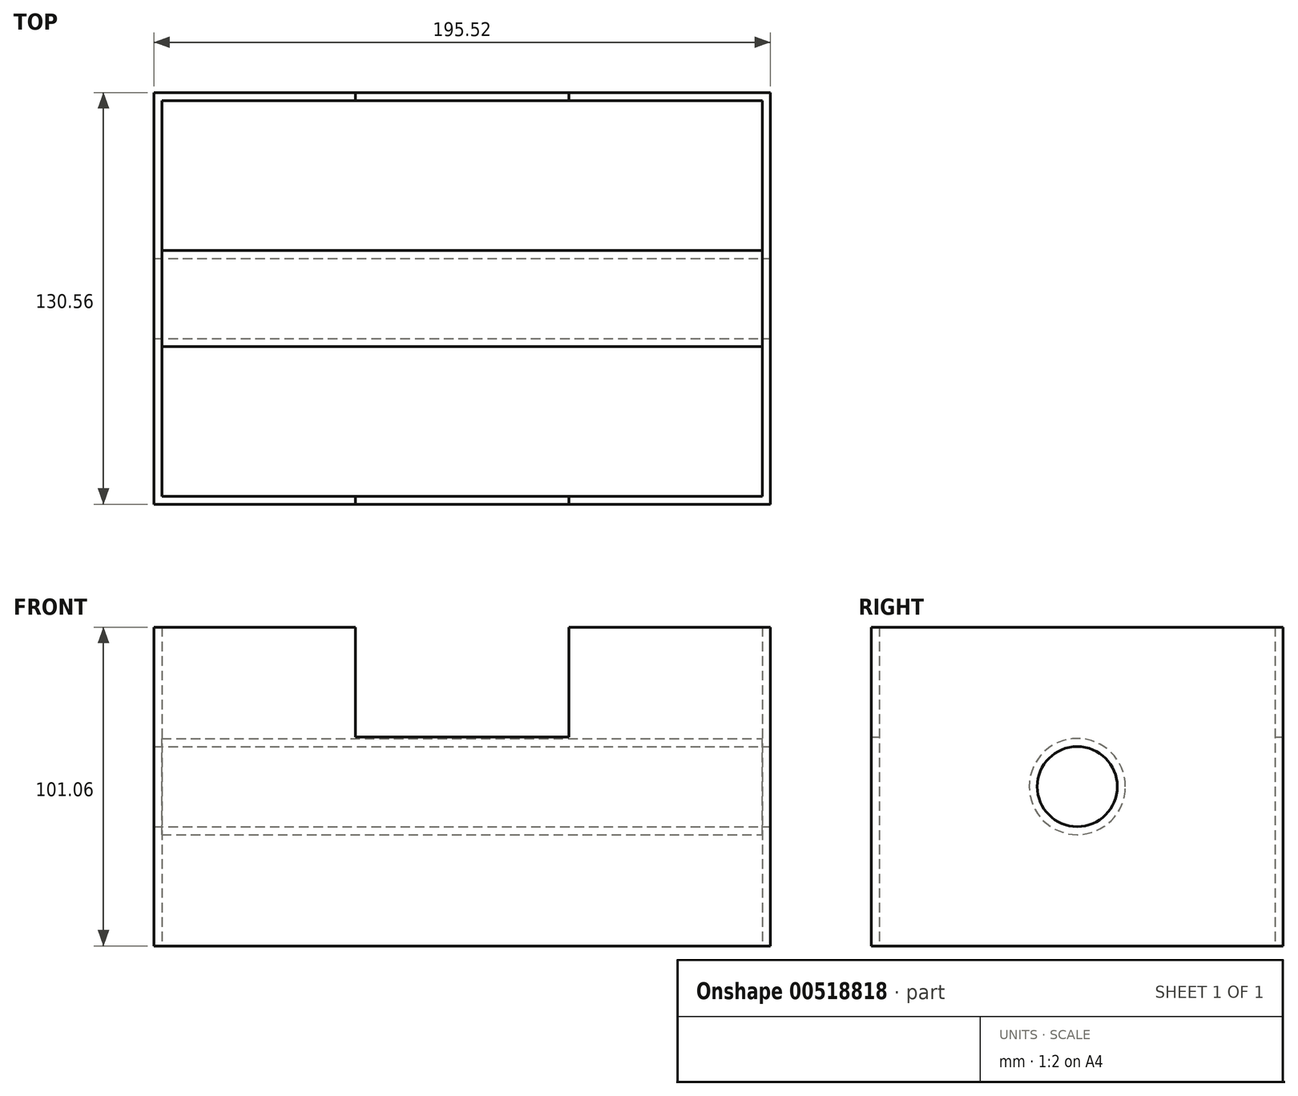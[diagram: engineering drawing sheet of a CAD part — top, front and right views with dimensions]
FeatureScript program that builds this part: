
annotation { "Feature Type Name" : "Feature", "Feature Type Description" : "" }
export const myFeature = defineFeature(function(context is Context, id is Id, definition is map)
    precondition{}
    {
        {
            var Q0;
            Q0=qCreatedBy(makeId("Front.planeOp"),FACE);
            var sketch = newSketch(context, id + "F0", { "sketchPlane" : qUnion([Q0])});
            skLineSegment(sketch, "E0.bottom", {"start": v(-97.76, 50.53) * mm, "end": v(-33.82, 50.53) * mm});
            skLineSegment(sketch, "E0.top", {"start": v(-97.76, -50.53) * mm, "end": v(97.76, -50.53) * mm});
            skLineSegment(sketch, "E0.left", {"start": v(-97.76, 50.53) * mm, "end": v(-97.76, -50.53) * mm});
            skLineSegment(sketch, "E0.right", {"start": v(97.76, 50.53) * mm, "end": v(97.76, -50.53) * mm});
            skPoint(sketch, "E0.middle", {"position": v(0, 0) * mm});
            skLineSegment(sketch, "E1.bottom", {"start": v(33.82, 50.53) * mm, "end": v(34.73, 50.53) * mm});
            skLineSegment(sketch, "E2.top", {"start": v(33.82, 15.69) * mm, "end": v(-33.9, 15.69) * mm});
            skLineSegment(sketch, "E2.left", {"start": v(33.82, 50.53) * mm, "end": v(33.82, 15.69) * mm});
            skLineSegment(sketch, "E2.right", {"start": v(-33.9, 50.53) * mm, "end": v(-33.9, 15.69) * mm});
            skLineSegment(sketch, "E3.trimOffspring", {"start": v(-33.82, 50.53) * mm, "end": v(-33.9, 50.53) * mm});
            skPoint(sketch, "E4.start.orphan", {"position": v(0, 50.53) * mm});
            skLineSegment(sketch, "E5.trimOffspring", {"start": v(34.73, 50.53) * mm, "end": v(97.76, 50.53) * mm});
            skSolve(sketch);
        }
        {
            var Q0;
            Q0 = qSketchRegion(id + "F0", true);
            extrude(context, id + "F1", {"entities" : qUnion([Q0]), "endBound" : BoundingType.SYMMETRIC, "depth" : 130.56 * mm, "offsetDistance" : 25.4 * mm});
        }
        {
            var Q0;
            Q0=makeQuery(id+"F1.opExtrude","SWEPT_FACE",FACE,{"disambiguationData":[OSD([sQuery(id+"F0.wireOp",EDGE,"E0.right")])]});
            var sketch = newSketch(context, id + "F2", { "sketchPlane" : qUnion([Q0])});
            skPoint(sketch, "E6", {"position": v(0, 0) * mm});
            skSolve(sketch);
        }
        {
            var Q0;
            Q0=sQuery(id+"F2.wireOp",VERTEX,"E6");
            var Q1;
            Q1=makeQuery(id+"F1.opExtrude","SWEPT_BODY",BODY,{"disambiguationData":[OSD([sQuery(id+"F0.wireOp",EDGE,"E0.bottom"),sQuery(id+"F0.wireOp",EDGE,"E0.top"),sQuery(id+"F0.wireOp",EDGE,"E0.left"),sQuery(id+"F0.wireOp",EDGE,"E0.right"),sQuery(id+"F0.wireOp",EDGE,"E1.bottom"),sQuery(id+"F0.wireOp",EDGE,"E2.top"),sQuery(id+"F0.wireOp",EDGE,"E2.left"),sQuery(id+"F0.wireOp",EDGE,"E2.right"),sQuery(id+"F0.wireOp",EDGE,"E5.trimOffspring")])]});
            hole(context, id + "F3", {"style" : HoleStyle.SIMPLE, "endStyle" : HoleEndStyle.THROUGH, "holeDiameter" : 25.4 * mm, "isTappedThrough" : true, "tappedDepth" : 12.7 * mm, "tapClearance" : 3, "locations" : qUnion([Q0]), "scope" : qUnion([Q1])});
        }
        {
            var Q0;
            Q0=makeQuery(id+"F1.opExtrude","SWEPT_FACE",FACE,{"disambiguationData":[OSD([sQuery(id+"F0.wireOp",EDGE,"E0.bottom")])]});
            var Q1;
            Q1=makeQuery(id+"F1.opExtrude","SWEPT_FACE",FACE,{"disambiguationData":[OSD([sQuery(id+"F0.wireOp",EDGE,"E2.top")])]});
            var Q2;
            Q2=makeQuery(id+"F1.opExtrude","SWEPT_FACE",FACE,{"disambiguationData":[OSD([sQuery(id+"F0.wireOp",EDGE,"E2.right")])]});
            var Q3;
            Q3=makeQuery(id+"F1.opExtrude","SWEPT_FACE",FACE,{"disambiguationData":[OSD([sQuery(id+"F0.wireOp",EDGE,"E1.bottom"),sQuery(id+"F0.wireOp",EDGE,"E5.trimOffspring")])]});
            var Q4;
            Q4=makeQuery(id+"F1.opExtrude","SWEPT_FACE",FACE,{"disambiguationData":[OSD([sQuery(id+"F0.wireOp",EDGE,"E2.left")])]});
            var Q5;
            Q5=makeQuery(id+"F3.hole-0.boolean.opBoolean","COPY",FACE,{"derivedFrom":makeQuery(id+"F3.hole-0.opRevolve","SWEPT_FACE",FACE,{"disambiguationData":[OSD([sQuery(id+"F3.hole-0.sketch.wireOp",EDGE,"core_line_2")])]})});
            var Q6;
            Q6=makeQuery(id+"F1.opExtrude","SWEPT_FACE",FACE,{"disambiguationData":[OSD([sQuery(id+"F0.wireOp",EDGE,"E0.top")])]});
            shell(context, id + "F4", {"entities" : qUnion([Q0, Q1, Q2, Q3, Q4, Q5, Q6]), "thickness" : 2.54 * mm});
        }
    });
